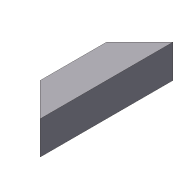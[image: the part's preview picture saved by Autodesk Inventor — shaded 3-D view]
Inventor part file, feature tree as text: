
AUTODESK INVENTOR PART (.ipt)
format: ipt  version: 2012 (Build 160160000, 160)  size: 84,480 bytes
history: native  units: in
note: dims shown in document units (in); Inventor stores cm internally (conversion verified against a paired STEP export)
features: extrude x2, sketch x2, shell x1
ambient origin geometry x8: Origin, YZ Plane, XZ Plane, XY Plane, X Axis, Y Axis, Z Axis, Center Point
bodies: Solid1 (feature_tree)
feature tree (5):
  extrude  "Extrusion1"  Depth=1.0in
  shell  "Shell1"  Thickness=4.0in
  extrude  "Extrusion2"  TaperAngle=45.0deg  [1 undecoded]
  sketch  "Sketch1"  dims[d0=1.0in d1=1.0in d2=4.0in d3=0.0in]
  sketch  "Sketch2"  dims[d4=0.0625in d5=45.0deg d6=45.0deg d7=4.0in d8=0.0in]
note: 1 required parameter value undecoded (feature->parameter linkage not recoverable at this tier; creation-order binding heuristic only, values carry confidence <= 0.55)
